# Revit family: T100001
name_source: partatom
category: Furniture
revit_build: Autodesk Revit Architecture 2013 (Build: 20120221_2030(x64)
units: mm (PartAtom-declared; Revit-internal decimal feet)

## types (1)
- T100001
    Assembly Code = E2020200
    Back Coverage Material = OFS BRANDS SLATE Back Coverage Plastic
    Catalog = http://ofsbrands.com
    Chassis Material = OFS BRANDS SLATE Chassis Wood
    Depth = 113 1/4"
    Description = OFS BRANDS OFS SLATE TYPICAL T100001
    Drawer Front Material = OFS BRANDS SLATE Drawer Front Wood
    Glides Material = OFS BRANDS SLATE Glide Plastic
    Grommet  Material = OFS BRANDS SLATE Grommet Metal
    Height = 68 3/4"
    Lock Material = OFS BRANDS SLATE Lock Metal
    Manufacturer = OFS
    Model = T100001
    Pull Material = OFS BRANDS SLATE Pull Metal
    Top Core Material = OFS BRANDS SLATE Top Core Wood
    URL = http://www.ofsbrands.com
    Width = 96"

## geometry (parser evidence)
native form markers: Blend x2, Sweep x1
no freeform markers — native parametric forms only
